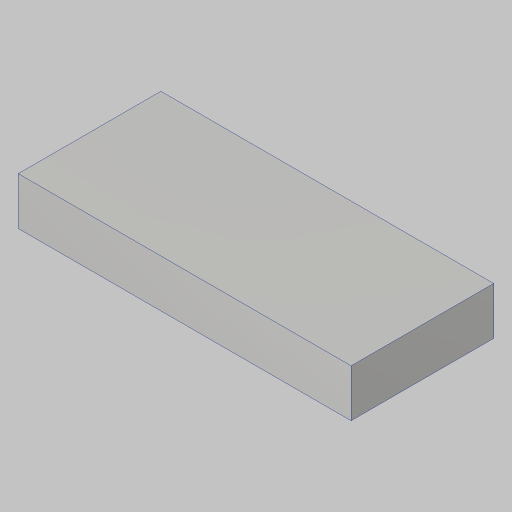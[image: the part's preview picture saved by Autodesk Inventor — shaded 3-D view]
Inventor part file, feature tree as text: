
AUTODESK INVENTOR PART (.ipt)
format: ipt  version: 2023.5 (Build 275446000, 446)  size: 88,064 bytes
history: native  units: in
note: dims shown in document units (in); Inventor stores cm internally (conversion verified against a paired STEP export)
features: extrude x1, sketch x1
ambient origin geometry x8: Origin, YZ Plane, XZ Plane, XY Plane, X Axis, Y Axis, Z Axis, Center Point
bodies: Solid1 (feature_tree)
feature tree (2):
  extrude  "Extrusion1"  Depth=6.0in
  sketch  "Sketch1"  dims[d0=14.0in d1=6.0in d2=2.0in d3=0.0in]
